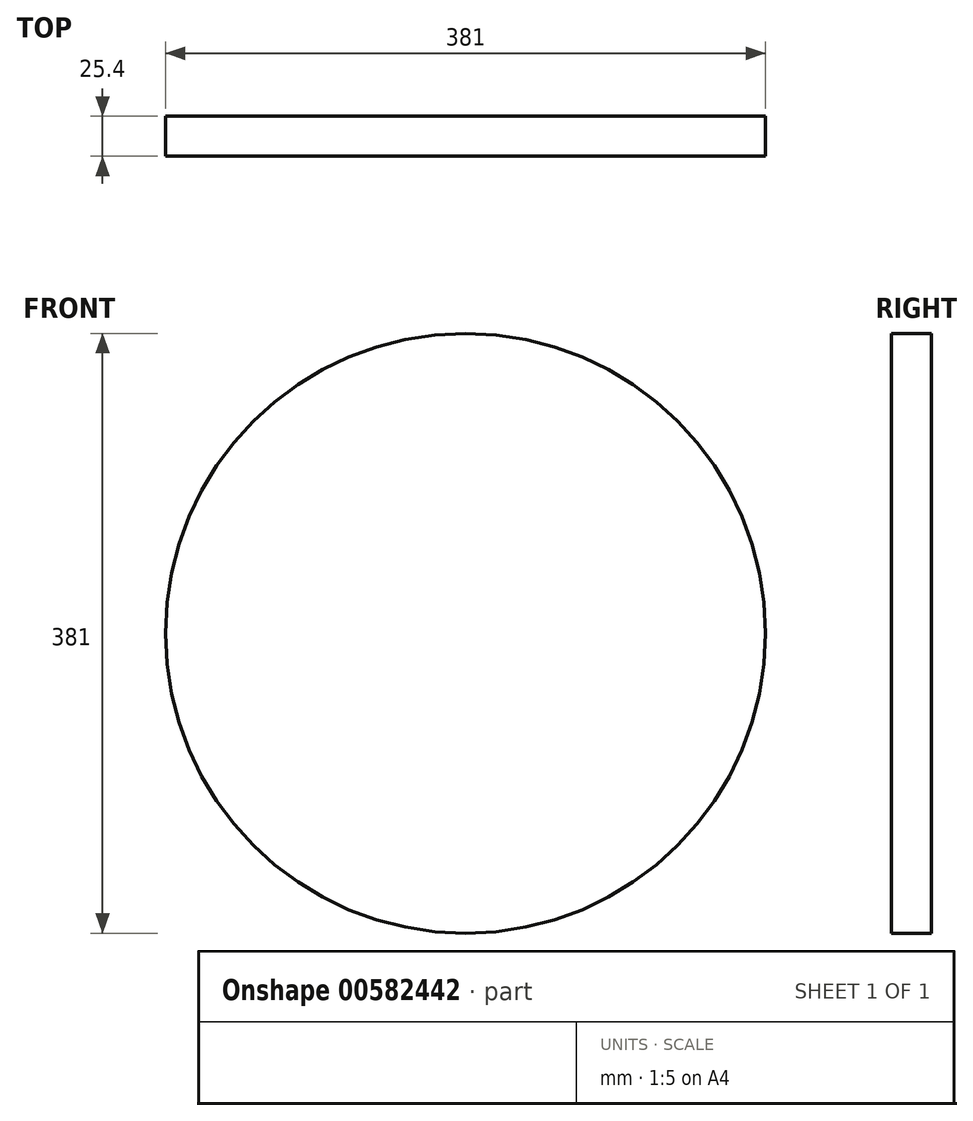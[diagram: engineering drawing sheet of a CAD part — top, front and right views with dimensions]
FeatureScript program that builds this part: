
annotation { "Feature Type Name" : "Feature", "Feature Type Description" : "" }
export const myFeature = defineFeature(function(context is Context, id is Id, definition is map)
    precondition{}
    {
        {
            var Q0;
            Q0=qCreatedBy(makeId("Front.planeOp"),FACE);
            var sketch = newSketch(context, id + "F0", { "sketchPlane" : qUnion([Q0])});
            skCircle(sketch, "E0", {"center": v(0, 0) * mm, "radius": 190.5 * mm});
            skSolve(sketch);
        }
        {
            var Q0;
            Q0=makeQuery(id+"F0.imprint","IMPRINT",FACE,{"disambiguationData":[TD([[makeQuery(id+"F0.imprint","IMPRINT",EDGE,{"derivedFrom":sQuery(id+"F0.wireOp",EDGE,"E0")}),1.0]])]});
            extrude(context, id + "F1", {"entities" : qUnion([Q0]), "endBound" : BoundingType.SYMMETRIC, "depth" : 25.4 * mm, "offsetDistance" : 25.4 * mm});
        }
    });
